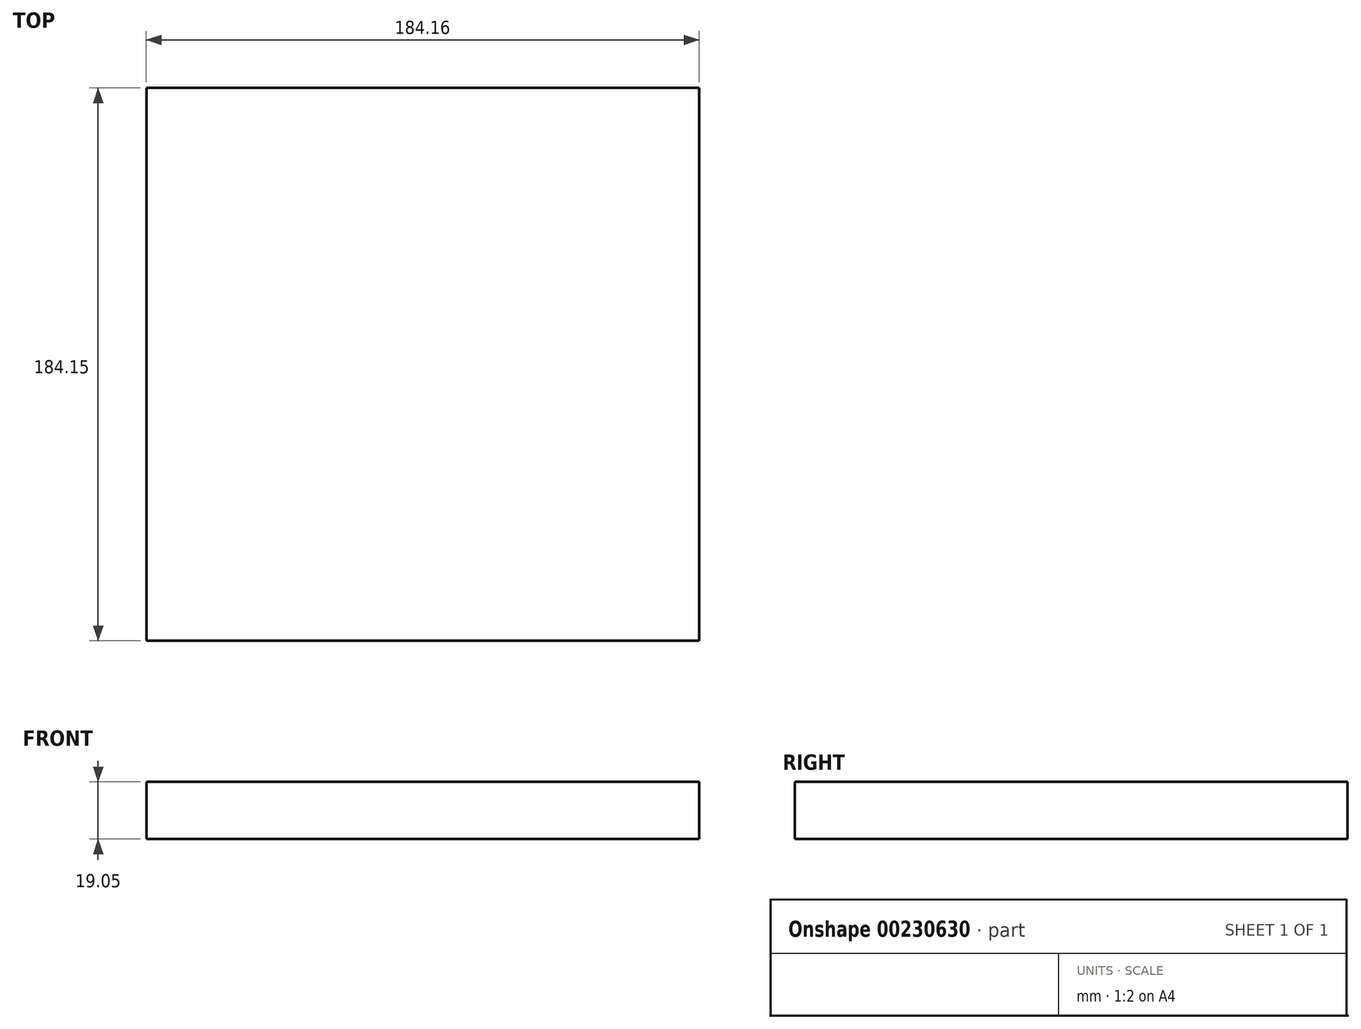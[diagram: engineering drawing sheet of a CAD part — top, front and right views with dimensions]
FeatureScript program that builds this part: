
annotation { "Feature Type Name" : "Feature", "Feature Type Description" : "" }
export const myFeature = defineFeature(function(context is Context, id is Id, definition is map)
    precondition{}
    {
        {
            var Q0;
            Q0=qCreatedBy(makeId("Top.planeOp"),FACE);
            var sketch = newSketch(context, id + "F0", { "sketchPlane" : qUnion([Q0])});
            skLineSegment(sketch, "E0.bottom", {"start": v(-92.07, 88.44) * mm, "end": v(92.08, 88.44) * mm});
            skLineSegment(sketch, "E0.top", {"start": v(-92.08, -95.71) * mm, "end": v(92.07, -95.71) * mm});
            skLineSegment(sketch, "E0.left", {"start": v(-92.07, 88.44) * mm, "end": v(-92.08, -95.71) * mm});
            skLineSegment(sketch, "E0.right", {"start": v(92.08, 88.44) * mm, "end": v(92.07, -95.71) * mm});
            skPoint(sketch, "E0.middle", {"position": v(0, -3.64) * mm});
            skSolve(sketch);
        }
        {
            var Q0;
            Q0 = qSketchRegion(id + "F0", true);
            extrude(context, id + "F1", {"entities" : qUnion([Q0]), "depth" : 19.05 * mm});
        }
    });
